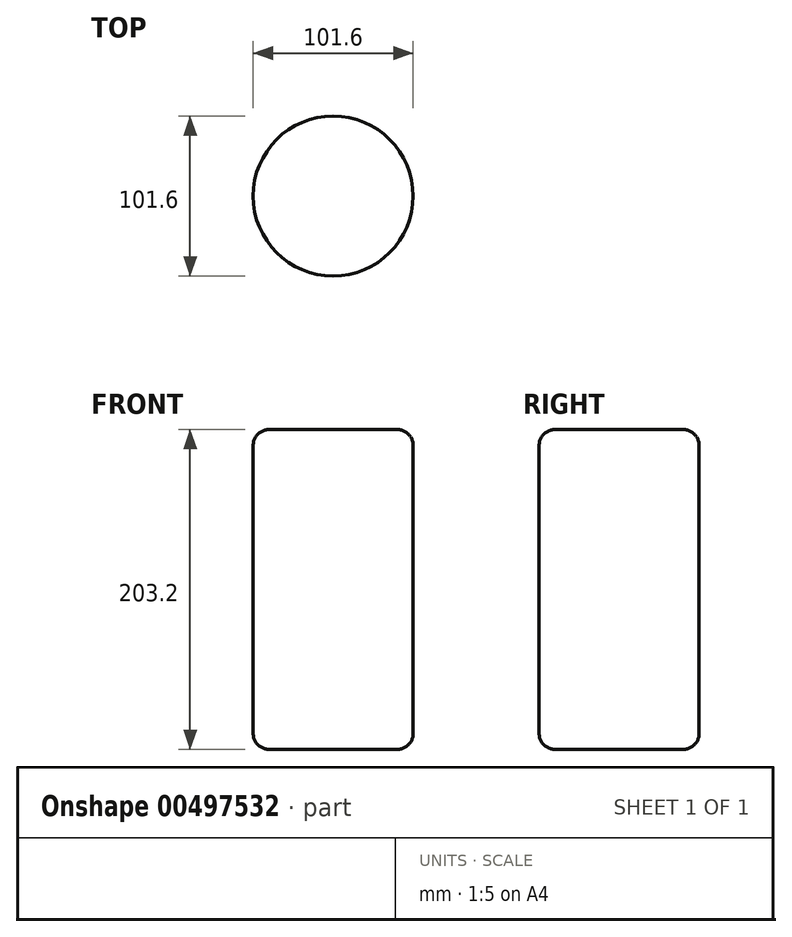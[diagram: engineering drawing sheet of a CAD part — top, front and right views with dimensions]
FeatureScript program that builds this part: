
annotation { "Feature Type Name" : "Feature", "Feature Type Description" : "" }
export const myFeature = defineFeature(function(context is Context, id is Id, definition is map)
    precondition{}
    {
        {
            var Q0;
            Q0=qCreatedBy(makeId("Top.planeOp"),FACE);
            var sketch = newSketch(context, id + "F0", { "sketchPlane" : qUnion([Q0])});
            skCircle(sketch, "E0", {"center": v(0, 0) * mm, "radius": 50.8 * mm});
            skSolve(sketch);
        }
        {
            var Q0;
            Q0=makeQuery(id+"F0.imprint","IMPRINT",FACE,{"disambiguationData":[TD([[makeQuery(id+"F0.imprint","IMPRINT",EDGE,{"derivedFrom":sQuery(id+"F0.wireOp",EDGE,"E0")}),1.0]])]});
            extrude(context, id + "F1", {"entities" : qUnion([Q0]), "depth" : 203.2 * mm});
        }
        {
            var Q0;
            Q0=makeQuery(id+"F1.opExtrude","CAP_FACE",FACE,{"disambiguationData":[OSD([sQuery(id+"F0.wireOp",EDGE,"E0")])],"isStart":true});
            fillet(context, id + "F2", {"entities" : qUnion([Q0]), "radius" : 10.16 * mm, "tangentPropagation" : true, "allowEdgeOverflow" : false});
        }
        {
            var Q0;
            Q0=makeQuery(id+"F1.opExtrude","CAP_EDGE",EDGE,{"disambiguationData":[OSD([sQuery(id+"F0.wireOp",EDGE,"E0")])],"isStart":false});
            fillet(context, id + "F3", {"entities" : qUnion([Q0]), "radius" : 10.16 * mm, "tangentPropagation" : true, "allowEdgeOverflow" : false});
        }
    });
